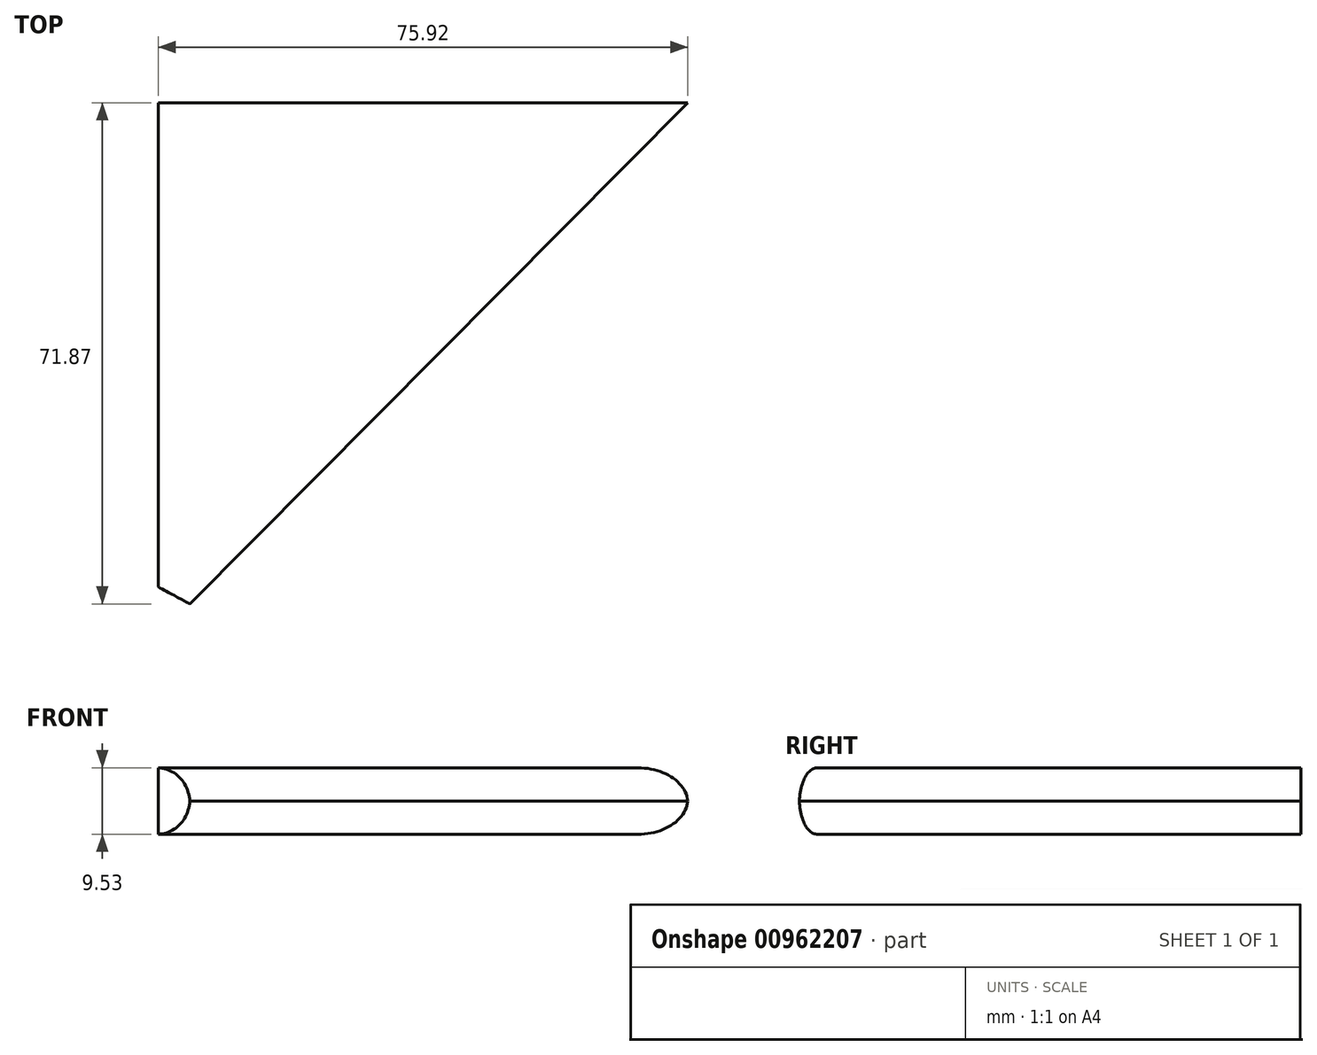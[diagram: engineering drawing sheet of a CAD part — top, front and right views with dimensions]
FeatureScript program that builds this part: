
annotation { "Feature Type Name" : "Feature", "Feature Type Description" : "" }
export const myFeature = defineFeature(function(context is Context, id is Id, definition is map)
    precondition{}
    {
        {
            var Q0;
            Q0=qCreatedBy(makeId("Top.planeOp"),FACE);
            var sketch = newSketch(context, id + "F0", { "sketchPlane" : qUnion([Q0])});
            skLineSegment(sketch, "E0", {"start": v(0, 0) * mm, "end": v(0, 76.55) * mm});
            skLineSegment(sketch, "E1", {"start": v(0, 76.55) * mm, "end": v(75.93, 76.55) * mm});
            skLineSegment(sketch, "E2", {"start": v(75.93, 76.55) * mm, "end": v(4.55, 4.68) * mm});
            skLineSegment(sketch, "E3", {"start": v(4.55, 4.68) * mm, "end": v(0, 7.14) * mm});
            skSolve(sketch);
        }
        {
            var Q0;
            {var subQ0=sQuery(id+"F0.wireOp",EDGE,"E1");Q0=makeQuery(id+"F0.imprint","IMPRINT",FACE,{"disambiguationData":[TD([[makeQuery(id+"F0.imprint","IMPRINT",EDGE,{"derivedFrom":subQ0}),-1.0]])]});}
            extrude(context, id + "F1", {"entities" : qUnion([Q0]), "depth" : 9.52 * mm, "offsetDistance" : 25.4 * mm});
        }
        {
            var Q0;
            Q0=makeQuery(id+"F1.opExtrude","CAP_EDGE",EDGE,{"disambiguationData":[OSD([sQuery(id+"F0.wireOp",EDGE,"E2")])],"isStart":true});
            var Q1;
            Q1=makeQuery(id+"F1.opExtrude","CAP_EDGE",EDGE,{"disambiguationData":[OSD([sQuery(id+"F0.wireOp",EDGE,"E2")])],"isStart":false});
            fillet(context, id + "F2", {"entities" : qUnion([Q0, Q1]), "radius" : 5.08 * mm, "tangentPropagation" : true, "allowEdgeOverflow" : false});
        }
    });
